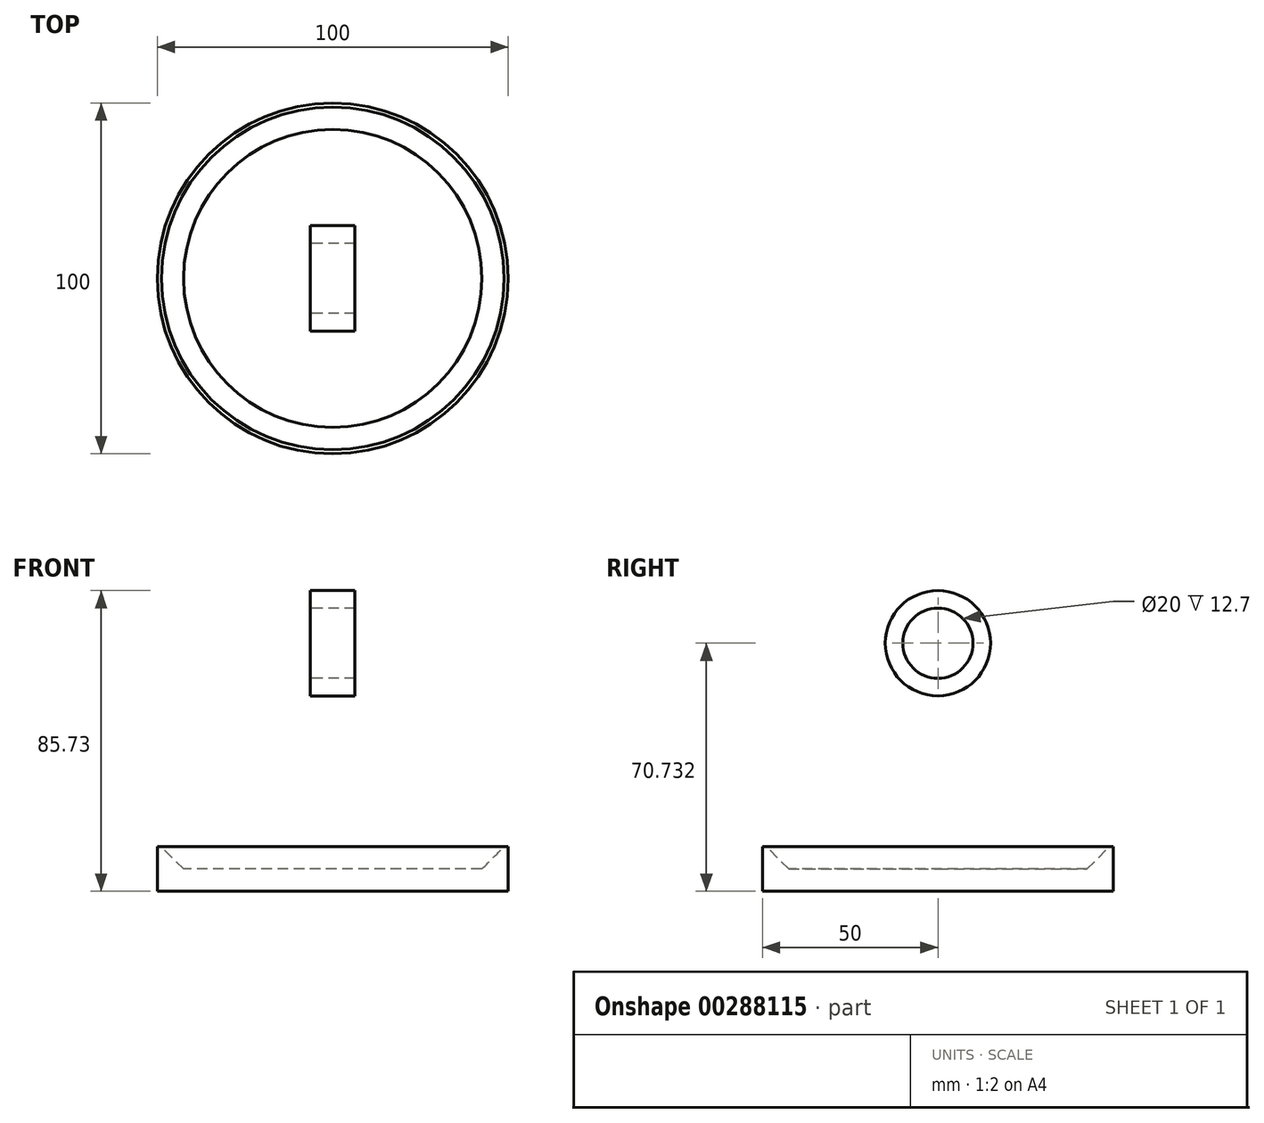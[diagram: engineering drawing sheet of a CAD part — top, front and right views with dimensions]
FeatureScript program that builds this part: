
annotation { "Feature Type Name" : "Feature", "Feature Type Description" : "" }
export const myFeature = defineFeature(function(context is Context, id is Id, definition is map)
    precondition{}
    {
        {
            var Q0;
            Q0=qCreatedBy(makeId("Top.planeOp"),FACE);
            var sketch = newSketch(context, id + "F0", { "sketchPlane" : qUnion([Q0])});
            skCircle(sketch, "E0", {"center": v(0, 0) * mm, "radius": 50 * mm});
            skSolve(sketch);
        }
        {
            var Q0;
            Q0 = qSketchRegion(id + "F0", true);
            extrude(context, id + "F1", {"entities" : qUnion([Q0]), "depth" : 6.35 * mm});
        }
        {
            var Q0;
            Q0=makeQuery(id+"F1.opExtrude","CAP_FACE",FACE,{"disambiguationData":[OSD([sQuery(id+"F0.wireOp",EDGE,"E0")])],"isStart":false});
            var sketch = newSketch(context, id + "F2", { "sketchPlane" : qUnion([Q0])});
            skCircle(sketch, "E1", {"center": v(0, 0) * mm, "radius": 42.5 * mm});
            skSolve(sketch);
        }
        {
            var Q0;
            Q0=makeQuery(id+"F2.imprint","IMPRINT",FACE,{"disambiguationData":[TD([[makeQuery(id+"F2.imprint","IMPRINT",EDGE,{"derivedFrom":sQuery(id+"F2.wireOp",EDGE,"E1")}),-1.0]])]});
            extrude(context, id + "F3", {"entities" : qUnion([Q0]), "operationType" : NewBodyOperationType.ADD, "depth" : 6.35 * mm});
        }
        {
            var Q0;
            Q0=makeQuery(id+"F3.opExtrude","CAP_EDGE",EDGE,{"disambiguationData":[OSD([sQuery(id+"F2.wireOp",EDGE,"E1")])],"isStart":false});
            chamfer(context, id + "F4", {"entities" : qUnion([Q0]), "width" : 6.35 * mm, "tangentPropagation" : true});
        }
        {
            var Q0;
            Q0=qCreatedBy(makeId("Right.planeOp"),FACE);
            var sketch = newSketch(context, id + "F5", { "sketchPlane" : qUnion([Q0])});
            skCircle(sketch, "E2", {"center": v(0, 70.73) * mm, "radius": 10 * mm});
            skCircle(sketch, "E3", {"center": v(0, 70.73) * mm, "radius": 15 * mm});
            skSolve(sketch);
        }
        {
            var Q0;
            Q0=makeQuery(id+"F5.imprint","IMPRINT",FACE,{"disambiguationData":[TD([[makeQuery(id+"F5.imprint","IMPRINT",EDGE,{"derivedFrom":sQuery(id+"F5.wireOp",EDGE,"E2")}),-1.0]])]});
            extrude(context, id + "F6", {"entities" : qUnion([Q0]), "endBound" : BoundingType.SYMMETRIC, "depth" : 12.7 * mm});
        }
    });
